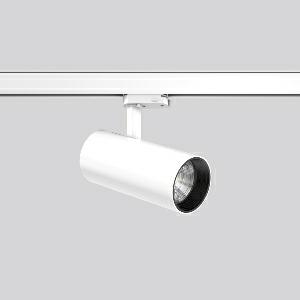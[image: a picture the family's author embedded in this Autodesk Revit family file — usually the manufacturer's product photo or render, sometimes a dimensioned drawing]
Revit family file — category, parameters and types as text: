
# Revit family: deecos_s_mini_742209_002_3_0ba9
name_source: partatom
category: Lighting Fixtures
units: mm (PartAtom-declared; Revit-internal decimal feet)

## family parameters
Cut with Voids When Loaded = No
Host = Face
Light Source = No
Part Type = Normal
Room Calculation Point = No
Round Connector Dimension = Use Diameter
Shared = No

## types (1)
- DEECOS S mini (1 x LED Modul 935, 3300 lm, 3500)
    Apparent Load = 29 VA
    Approval mark = CE
    CIE Flux Codes = 80 99 100 100 100
    Color Rendering = 92
    Color Temperature = 3500
    Default Elevation = 1800 mm
    Description = Series: DEECOS S mini
LED surface-mounted projector in modern design with no visible cooling ribs. Housing: die-cast aluminium, powder-coated. Rotation range: 356°. Swivel range: 90°. Black plastic ring and recessed LED to prevent glare from the side. Optical assembly with lens made of plastic (polycarbonate) for the best homogeneous light distribution - can be changed without tools. Best colour rendering index Ra>90. With multi adaptor for 3-circuit tracks 230 V. Suitable for Track on ceiling, Wall track. High quality converter without flickering and stroboscopic effect. The following accessories can be mounted without use of tools: interchangeable lenses, decorative glasses, honeycomb louvre, clear and frosted diffusers, white interchangeable plastic ring. 
Colour: traffic white, matt (RAL 9016)
Diameter: 87 mm
Height: 214 mm
Lamp: LED
Socket: without socket
Colour temperature: 3500K
Colour rendering index (CRI): 92
System power: 29 W
Rated luminous flux: 3300 lm
Luminous efficiency: 114 lm/W
Control gear: Regulated power supply
Protection class: I
Type of protection: IP 20
    Height = 214 mm
    Lamp = 1 x LED Modul 935
    Lamp Light Flux = 3300 lm
    Lamp count = 1
    Length = 87 mm
    Lifetime = 50000 h
    Luminous efficacy = 114 lm/W
    Manufacturer = RZB
    ModVariant = No
    Model = 742209.002.3
    Mounting Place = Ceiling
    Mounting Type = Rail mounted
    Number of Poles = 1
    OnlyDefault = Yes
    Power Factor = 1
    Product Name = DEECOS S mini
    Product group = Track mounted projectors
    ProductGroupID = 301
    Protection Class = Protection class I
    Protection Degree = IP 20
    RLX_Detail_Level = 1
    RLX_Emergency_Light_Flux = 0 lm
    RLX_Emergency_Type = 0
    RLX_Emergency_Type_DB = No
    RlxData = <blob elided: 35797 chars, md5=f0f883e8>
    Socket = socket
    Standby Power = 0 W
    System Light Flux = 3300 lm
    System Power = 29 W
    Type Comments = Product without accessories
    Type Image = 741930.002.jpg
    URL = http://relux.com
    VarID = ---
    Voltage = 230 V
    Voltage Range = 220-240 V
    Weight = 0.00 kg
    Width = 0 mm  [stored 0 ft]

note: [stored X ft] marks values corroborated as IEEE doubles in the binary element streams (Revit-internal decimal feet)

## geometry (parser evidence)
native form markers: Blend x4, Sweep x14
no freeform markers — native parametric forms only
